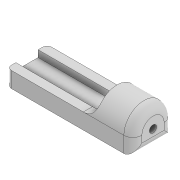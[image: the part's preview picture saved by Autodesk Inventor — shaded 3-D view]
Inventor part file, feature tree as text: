
AUTODESK INVENTOR PART (.ipt)
format: ipt  version: 2022 (Build 260153000, 153)  size: 150,528 bytes
history: native  units: mm
features: extrude x3, fillet x3, sketch x3, projected_geometry x1
ambient origin geometry x8: Origin, YZ Plane, XZ Plane, XY Plane, X Axis, Y Axis, Z Axis, Center Point
bodies: Solid1 (feature_tree)
feature tree (10):
  extrude  "Extrusion1"  Depth=2.0mm
  extrude  "Extrusion2"  Depth=2.475mm
  extrude  "Extrusion3"  Depth=1.5mm
  fillet  "Fillet1"  Radius=20.0mm
  fillet  "Fillet2"  Radius=8.0mm
  fillet  "Fillet3"  Radius=1.6mm
  sketch  "Sketch1"  dims[d0=2.0mm d1=2.0mm]
  sketch  "Sketch2"  dims[d2=2.0mm d4=2.475mm]
  projected_geometry  "Projected Loop1"
  sketch  "Sketch3"  dims[d5=2.475mm d6=1.5mm d7=20.0mm d8=0.0mm d9=8.0mm d10=0.0mm d11=1.6mm d12=10.0mm d13=0.0mm d14=3.0mm d15=2.0mm d16=1.0mm d17=1.5mm]
